# Revit family: Haworth_Atwell_TandemSeating
name_source: partatom
category: Furniture
revit_build: Autodesk Revit 2018 (Build: 20170223_1515(x64)
units: mm (PartAtom-declared; Revit-internal decimal feet)

## family parameters
Always vertical = Yes
Cut with Voids When Loaded = No
OmniClass Number = 23.40.20.00
OmniClass Title = General Furniture and Specialties
Room Calculation Point = No
Shared = No
Work Plane-Based = No

## types (8) — shared parameters
Actual Depth = 2' - 6"
Actual Height = 3' - 0"
Assembly Code = E2020200
Manufacturer = Haworth
Model = Haworth Atwell
Size = Verify Final Dim. w/ Haworth
Sustainability Info = https://www.haworth.com
URL = http://healthcare.haworth.com
URL - Product = http://healthcare.haworth.com
Version = 0
Warranty = http://healthcare.haworth.com

## per-type parameters (varying)
| type | Actual Number of Chairs | Actual Width | Array Center Arm | Array Chairs | Array Seat | Array without Center Arm | Center Arm | Description | Distance - Left to Center | Number of Chairs | Number of Chairs - Not Two | Number of Chairs - Two | Single Seat | Single Seat Center Arm | Single Seat No Center Arm | Without Center Arm |
| HE902-T2-C - 50w | 2 | 3' - 10 3/4" | No | 2 | No | No | Yes | Tandem Seating - 2 Chair | 2' - 0 5/8" | 2 | No | Yes | Yes | Yes | No | No |
| HE902-T2-N - 50w | 2 | 3' - 10 3/4" | No | 2 | No | No | No | Tandem Seating - 2 Chair | 2' - 0 5/8" | 2 | No | Yes | Yes | No | Yes | Yes |
| HE903-T3-C - 72.5w | 3 | 6' - 1" | Yes | 2 | Yes | No | Yes | Tandem Seating - 3 Chair | 3' - 0 1/2" | 3 | Yes | No | No | No | No | No |
| HE903-T3-N - 72.5w | 3 | 6' - 1" | No | 2 | Yes | Yes | No | Tandem Seating - 3 Chair | 3' - 0 1/2" | 3 | Yes | No | No | No | No | Yes |
| HE904-T4-C - 96w | 4 | 8' - 0 3/4" | Yes | 3 | Yes | No | Yes | Tandem Seating - 4 Chair | 4' - 0 3/8" | 4 | Yes | No | No | No | No | No |
| HE904-T4-N - 96w | 4 | 8' - 0 3/4" | No | 3 | Yes | Yes | No | Tandem Seating - 4 Chair | 4' - 0 3/8" | 4 | Yes | No | No | No | No | Yes |
| HE905-T5-C - 119.5w | 5 | 10' - 0 1/2" | Yes | 4 | Yes | No | Yes | Tandem Seating - 5 Chair | 5' - 0 1/4" | 5 | Yes | No | No | No | No | No |
| HE905-T5-N - 119.5w | 5 | 10' - 0 1/2" | No | 4 | Yes | Yes | No | Tandem Seating - 5 Chair | 5' - 0 1/4" | 5 | Yes | No | No | No | No | Yes |

## geometry (parser evidence)
native form markers: Sweep x13
no freeform markers — native parametric forms only
